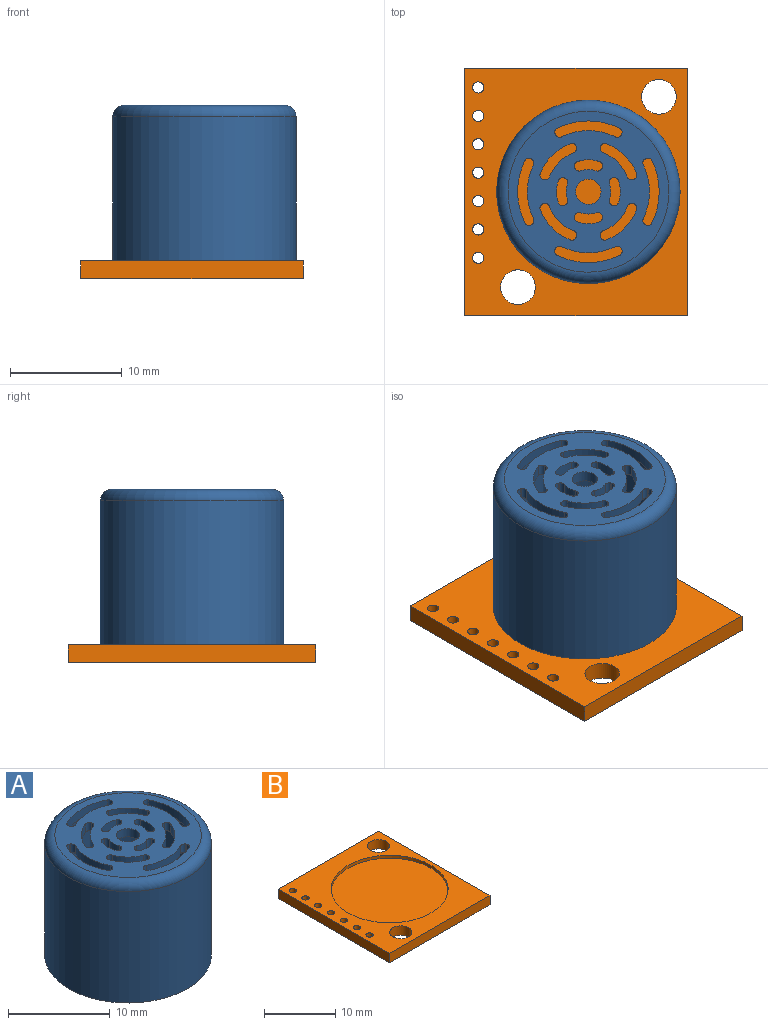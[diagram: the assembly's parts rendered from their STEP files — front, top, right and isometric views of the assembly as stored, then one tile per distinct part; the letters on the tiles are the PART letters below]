
ASSEMBLY  parts=2 mates=1
PART A: 103 faces, bbox 17.8x17.8x14.4 mm
  f0: plane 14.4x14.4mm, normal (0,0,-1), area 115.1mm2, adj f4,f6,f7,f8,f9,f10,f11,f12
  f1: plane 14.4x14.4mm, normal (0,0,1), area 115.1mm2, adj f5,f6,f7,f8,f9,f10,f11,f12
  f2: cylinder r=8.2mm len=16.4mm, axis (0,0,-1), area 690.4mm2, adj f3,f5
  f3: plane 16.4x16.4mm, normal (0,0,-1), area 48.4mm2, adj f2,f4
  f4: cylinder r=7.2mm len=14.4mm, axis (0,0,-1), area 606.2mm2, adj f0,f3
  f5: torus R=7.2mm, axis (0,0,1), area 77.3mm2, adj f1,f2
  f6: cylinder r=1.13mm len=2.26mm, axis (0,0,1), area 7.1mm2, adj f0,f1
  f7: plane 1x0.07mm, normal (-0.26,0.97,0), area 0.1mm2, adj f0,f1,f67,f68
  f8: cylinder r=3.73mm len=2.18mm, axis (0,0,1), area 3.2mm2, adj f0,f1,f67,f69
  f9: cylinder r=4.6mm len=2.7mm, axis (0,0,1), area 3.9mm2, adj f0,f1,f68,f70
  f10: plane 1x0.07mm, normal (0.97,-0.26,0), area 0.1mm2, adj f0,f1,f69,f70
  f11: plane 1x0.06mm, normal (-0.87,0.5,0), area 0.1mm2, adj f0,f1,f63,f64
  f12: cylinder r=6.33mm len=5.58mm, axis (0,0,1), area 5.8mm2, adj f0,f1,f64,f66
  f13: cylinder r=5.47mm len=4.81mm, axis (0,0,1), area 5mm2, adj f0,f1,f63,f65
  f14: plane 1x0.06mm, normal (0.87,0.5,0), area 0.1mm2, adj f0,f1,f65,f66
  f15: cylinder r=5.47mm len=4.81mm, axis (0,0,1), area 5mm2, adj f0,f1,f59,f60
  f16: plane 1x0.06mm, normal (0.87,-0.5,0), area 0.1mm2, adj f0,f1,f60,f62
  f17: plane 1x0.06mm, normal (-0.87,-0.5,0), area 0.1mm2, adj f0,f1,f59,f61
  f18: cylinder r=6.33mm len=5.58mm, axis (0,0,1), area 5.8mm2, adj f0,f1,f61,f62
  f19: cylinder r=5.47mm len=4.81mm, axis (0,0,1), area 5mm2, adj f0,f1,f55,f56
  f20: plane 1x0.06mm, normal (0.5,0.87,0), area 0.1mm2, adj f0,f1,f56,f58
  f21: plane 1x0.06mm, normal (0.5,-0.87,0), area 0.1mm2, adj f0,f1,f55,f57
  f22: cylinder r=6.33mm len=5.58mm, axis (0,0,1), area 5.8mm2, adj f0,f1,f57,f58
  f23: plane 1x0.06mm, normal (-0.87,0.5,0), area 0.1mm2, adj f0,f1,f87,f88
  f24: cylinder r=2.86mm len=2.02mm, axis (0,0,1), area 2.1mm2, adj f0,f1,f88,f90
  f25: cylinder r=2mm len=1.39mm, axis (0,0,1), area 1.4mm2, adj f0,f1,f87,f89
  f26: plane 1x0.06mm, normal (0.87,0.5,0), area 0.1mm2, adj f0,f1,f89,f90
  f27: cylinder r=6.33mm len=5.58mm, axis (0,0,1), area 5.8mm2, adj f0,f1,f91,f92
  f28: plane 1x0.06mm, normal (-0.5,-0.87,0), area 0.1mm2, adj f0,f1,f91,f93
  f29: plane 1x0.06mm, normal (-0.5,0.87,0), area 0.1mm2, adj f0,f1,f92,f94
  f30: cylinder r=5.47mm len=4.81mm, axis (0,0,1), area 5mm2, adj f0,f1,f93,f94
  f31: cylinder r=2.86mm len=2.02mm, axis (0,0,1), area 2.1mm2, adj f0,f1,f99,f100
  f32: plane 1x0.06mm, normal (-0.5,-0.87,0), area 0.1mm2, adj f0,f1,f99,f101
  f33: plane 1x0.06mm, normal (-0.5,0.87,0), area 0.1mm2, adj f0,f1,f100,f102
  f34: cylinder r=2mm len=1.39mm, axis (0,0,1), area 1.4mm2, adj f0,f1,f101,f102
  f35: cylinder r=4.6mm len=2.7mm, axis (0,0,1), area 3.9mm2, adj f0,f1,f95,f96
  f36: plane 1x0.07mm, normal (0.26,-0.97,0), area 0.1mm2, adj f0,f1,f95,f97
  f37: plane 1x0.07mm, normal (-0.97,0.26,0), area 0.1mm2, adj f0,f1,f96,f98
  f38: cylinder r=3.73mm len=2.18mm, axis (0,0,1), area 3.2mm2, adj f0,f1,f97,f98
  f39: plane 1x0.07mm, normal (0.97,0.26,0), area 0.1mm2, adj f0,f1,f71,f72
  f40: cylinder r=3.73mm len=2.18mm, axis (0,0,1), area 3.2mm2, adj f0,f1,f71,f73
  f41: cylinder r=4.6mm len=2.7mm, axis (0,0,1), area 3.9mm2, adj f0,f1,f72,f74
  f42: plane 1x0.07mm, normal (-0.26,-0.97,0), area 0.1mm2, adj f0,f1,f73,f74
  f43: cylinder r=4.6mm len=2.7mm, axis (0,0,1), area 3.9mm2, adj f0,f1,f75,f76
  f44: plane 1x0.07mm, normal (-0.97,-0.26,0), area 0.1mm2, adj f0,f1,f75,f77
  f45: plane 1x0.07mm, normal (0.26,0.97,0), area 0.1mm2, adj f0,f1,f76,f78
  f46: cylinder r=3.73mm len=2.18mm, axis (0,0,1), area 3.2mm2, adj f0,f1,f77,f78
  f47: cylinder r=2mm len=1.39mm, axis (0,0,1), area 1.4mm2, adj f0,f1,f79,f80
  f48: plane 1x0.06mm, normal (0.5,0.87,0), area 0.1mm2, adj f0,f1,f80,f82
  f49: plane 1x0.06mm, normal (0.5,-0.87,0), area 0.1mm2, adj f0,f1,f79,f81
  f50: cylinder r=2.86mm len=2.02mm, axis (0,0,1), area 2.1mm2, adj f0,f1,f81,f82
  f51: cylinder r=2mm len=1.39mm, axis (0,0,1), area 1.4mm2, adj f0,f1,f83,f84
  f52: plane 1x0.06mm, normal (0.87,-0.5,0), area 0.1mm2, adj f0,f1,f84,f86
  f53: plane 1x0.06mm, normal (-0.87,-0.5,0), area 0.1mm2, adj f0,f1,f83,f85
  f54: cylinder r=2.86mm len=2.02mm, axis (0,0,1), area 2.1mm2, adj f0,f1,f85,f86
  f55: cylinder r=0.4mm len=1mm, axis (0,0,1), area 0.6mm2, adj f0,f1,f19,f21
  f56: cylinder r=0.4mm len=1mm, axis (0,0,1), area 0.6mm2, adj f0,f1,f19,f20
  f57: cylinder r=0.4mm len=1mm, axis (0,0,1), area 0.7mm2, adj f0,f1,f21,f22
  f58: cylinder r=0.4mm len=1mm, axis (0,0,1), area 0.7mm2, adj f0,f1,f20,f22
  f59: cylinder r=0.4mm len=1mm, axis (0,0,1), area 0.6mm2, adj f0,f1,f15,f17
  f60: cylinder r=0.4mm len=1mm, axis (0,0,1), area 0.6mm2, adj f0,f1,f15,f16
  f61: cylinder r=0.4mm len=1mm, axis (0,0,1), area 0.7mm2, adj f0,f1,f17,f18
  f62: cylinder r=0.4mm len=1mm, axis (0,0,1), area 0.7mm2, adj f0,f1,f16,f18
  f63: cylinder r=0.4mm len=1mm, axis (0,0,1), area 0.6mm2, adj f0,f1,f11,f13
  f64: cylinder r=0.4mm len=1mm, axis (0,0,1), area 0.7mm2, adj f0,f1,f11,f12
  f65: cylinder r=0.4mm len=1mm, axis (0,0,1), area 0.6mm2, adj f0,f1,f13,f14
  f66: cylinder r=0.4mm len=1mm, axis (0,0,1), area 0.7mm2, adj f0,f1,f12,f14
  f67: cylinder r=0.4mm len=1mm, axis (0,0,1), area 0.6mm2, adj f0,f1,f7,f8
  f68: cylinder r=0.4mm len=1mm, axis (0,0,1), area 0.7mm2, adj f0,f1,f7,f9
  f69: cylinder r=0.4mm len=1mm, axis (0,0,1), area 0.6mm2, adj f0,f1,f8,f10
  f70: cylinder r=0.4mm len=1mm, axis (0,0,1), area 0.7mm2, adj f0,f1,f9,f10
  f71: cylinder r=0.4mm len=1mm, axis (0,0,1), area 0.6mm2, adj f0,f1,f39,f40
  f72: cylinder r=0.4mm len=1mm, axis (0,0,1), area 0.7mm2, adj f0,f1,f39,f41
  f73: cylinder r=0.4mm len=1mm, axis (0,0,1), area 0.6mm2, adj f0,f1,f40,f42
  f74: cylinder r=0.4mm len=1mm, axis (0,0,1), area 0.7mm2, adj f0,f1,f41,f42
  f75: cylinder r=0.4mm len=1mm, axis (0,0,1), area 0.7mm2, adj f0,f1,f43,f44
  f76: cylinder r=0.4mm len=1mm, axis (0,0,1), area 0.7mm2, adj f0,f1,f43,f45
  f77: cylinder r=0.4mm len=1mm, axis (0,0,1), area 0.6mm2, adj f0,f1,f44,f46
  f78: cylinder r=0.4mm len=1mm, axis (0,0,1), area 0.6mm2, adj f0,f1,f45,f46
  f79: cylinder r=0.4mm len=1mm, axis (0,0,1), area 0.6mm2, adj f0,f1,f47,f49
  f80: cylinder r=0.4mm len=1mm, axis (0,0,1), area 0.6mm2, adj f0,f1,f47,f48
  f81: cylinder r=0.4mm len=1mm, axis (0,0,1), area 0.7mm2, adj f0,f1,f49,f50
  f82: cylinder r=0.4mm len=1mm, axis (0,0,1), area 0.7mm2, adj f0,f1,f48,f50
  f83: cylinder r=0.4mm len=1mm, axis (0,0,1), area 0.6mm2, adj f0,f1,f51,f53
  f84: cylinder r=0.4mm len=1mm, axis (0,0,1), area 0.6mm2, adj f0,f1,f51,f52
  f85: cylinder r=0.4mm len=1mm, axis (0,0,1), area 0.7mm2, adj f0,f1,f53,f54
  f86: cylinder r=0.4mm len=1mm, axis (0,0,1), area 0.7mm2, adj f0,f1,f52,f54
  f87: cylinder r=0.4mm len=1mm, axis (0,0,1), area 0.6mm2, adj f0,f1,f23,f25
  f88: cylinder r=0.4mm len=1mm, axis (0,0,1), area 0.7mm2, adj f0,f1,f23,f24
  f89: cylinder r=0.4mm len=1mm, axis (0,0,1), area 0.6mm2, adj f0,f1,f25,f26
  f90: cylinder r=0.4mm len=1mm, axis (0,0,1), area 0.7mm2, adj f0,f1,f24,f26
  f91: cylinder r=0.4mm len=1mm, axis (0,0,1), area 0.7mm2, adj f0,f1,f27,f28
  f92: cylinder r=0.4mm len=1mm, axis (0,0,1), area 0.7mm2, adj f0,f1,f27,f29
  f93: cylinder r=0.4mm len=1mm, axis (0,0,1), area 0.6mm2, adj f0,f1,f28,f30
  f94: cylinder r=0.4mm len=1mm, axis (0,0,1), area 0.6mm2, adj f0,f1,f29,f30
  f95: cylinder r=0.4mm len=1mm, axis (0,0,1), area 0.7mm2, adj f0,f1,f35,f36
  f96: cylinder r=0.4mm len=1mm, axis (0,0,1), area 0.7mm2, adj f0,f1,f35,f37
  f97: cylinder r=0.4mm len=1mm, axis (0,0,1), area 0.6mm2, adj f0,f1,f36,f38
  f98: cylinder r=0.4mm len=1mm, axis (0,0,1), area 0.6mm2, adj f0,f1,f37,f38
  f99: cylinder r=0.4mm len=1mm, axis (0,0,1), area 0.7mm2, adj f0,f1,f31,f32
  f100: cylinder r=0.4mm len=1mm, axis (0,0,1), area 0.7mm2, adj f0,f1,f31,f33
  f101: cylinder r=0.4mm len=1mm, axis (0,0,1), area 0.6mm2, adj f0,f1,f32,f34
  f102: cylinder r=0.4mm len=1mm, axis (0,0,1), area 0.6mm2, adj f0,f1,f33,f34
PART B: 17 faces, bbox 19.9x22.1x1.6 mm
  f0: plane 19.9x1.6mm, normal (0,1,0), area 31.8mm2, adj f1,f12,f13,f14
  f1: plane 22.1x1.6mm, normal (-1,0,0), area 35.4mm2, adj f0,f2,f13,f14
  f2: plane 19.9x1.6mm, normal (0,-1,0), area 31.8mm2, adj f1,f12,f13,f14
  f3: cylinder r=1.55mm len=3.1mm, axis (0,0,-1), area 15.6mm2, adj f13,f14
  f4: cylinder r=1.55mm len=3.1mm, axis (0,0,-1), area 15.6mm2, adj f13,f14
  f5: cylinder r=0.5mm len=1.6mm, axis (0,0,-1), area 5mm2, adj f13,f14
  f6: cylinder r=0.5mm len=1.6mm, axis (0,0,-1), area 5mm2, adj f13,f14
  f7: cylinder r=0.5mm len=1.6mm, axis (0,0,-1), area 5mm2, adj f13,f14
  f8: cylinder r=0.5mm len=1.6mm, axis (0,0,-1), area 5mm2, adj f13,f14
  f9: cylinder r=0.5mm len=1.6mm, axis (0,0,-1), area 5mm2, adj f13,f14
  f10: cylinder r=0.5mm len=1.6mm, axis (0,0,-1), area 5mm2, adj f13,f14
  f11: cylinder r=0.5mm len=1.6mm, axis (0,0,-1), area 5mm2, adj f13,f14
  f12: plane 22.1x1.6mm, normal (1,0,0), area 35.4mm2, adj f0,f2,f13,f14
  f13: plane 22.1x19.9mm, normal (0,0,1), area 208mm2, adj f0,f1,f2,f3,f4,f5,f6,f7
  f14: plane 22.1x19.9mm, normal (0,0,-1), area 419.2mm2, adj f0,f1,f2,f3,f4,f5,f6,f7
  f15: cylinder r=8.2mm len=16.4mm, axis (0,0,1), area 25.8mm2, adj f13,f16
  f16: plane 16.4x16.4mm, normal (0,0,1), area 211.2mm2, adj f15
PLACE A t=(1.3,-3.14,-4.57)mm
PLACE B t=(-9.76,7.91,-5.67)mm fixed
MATE fastened A.f2 <-> B.f15  axis (0,0,-1) through (1.3,-3.14,-4.57)mm
